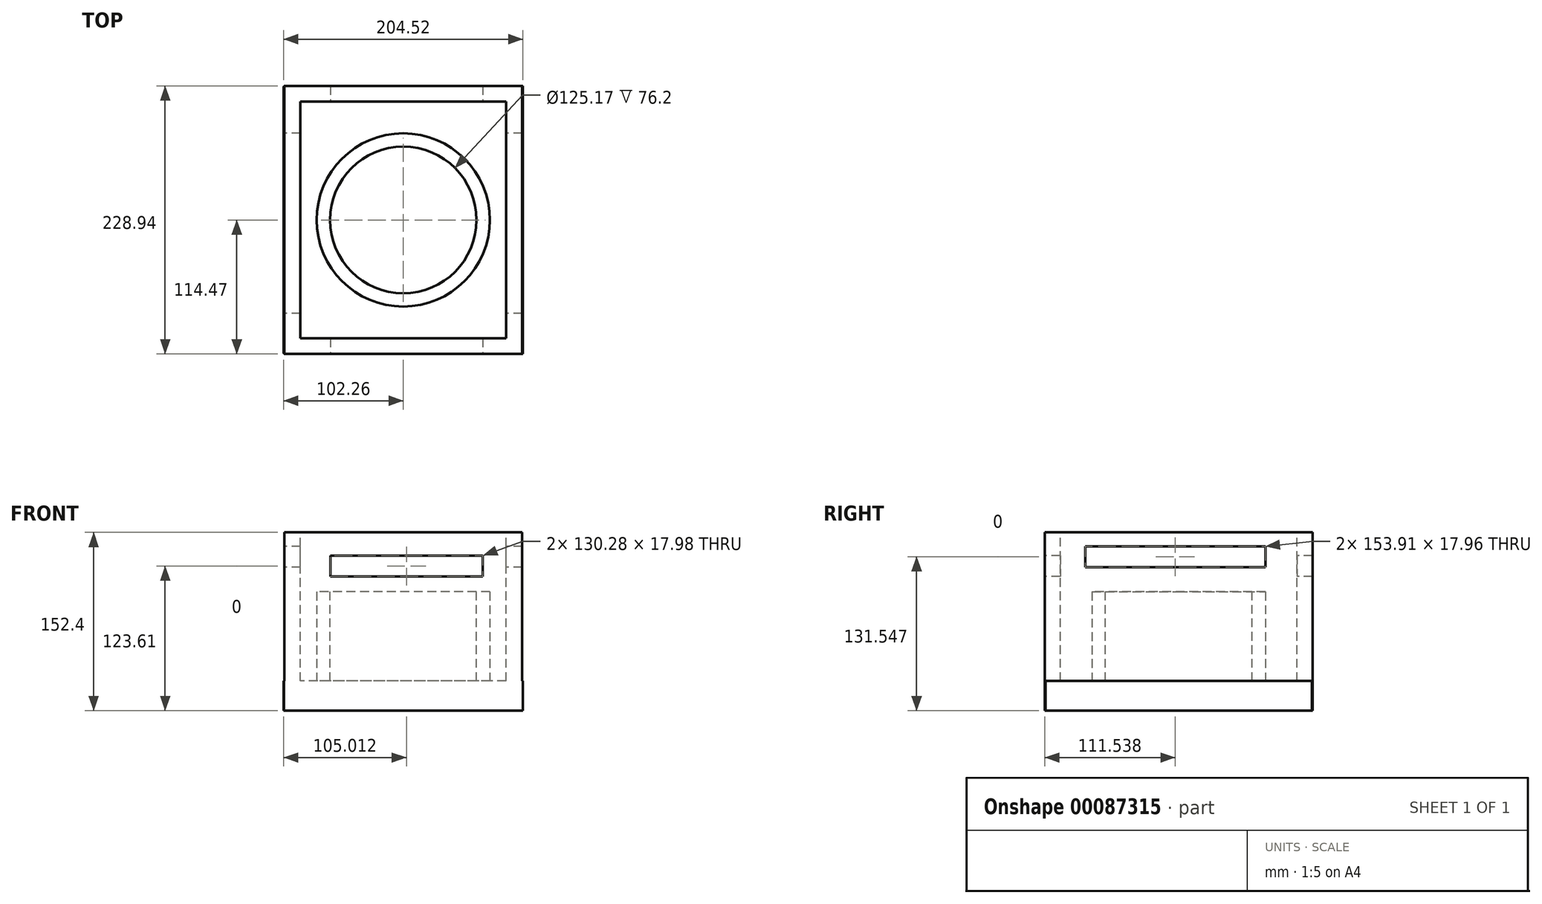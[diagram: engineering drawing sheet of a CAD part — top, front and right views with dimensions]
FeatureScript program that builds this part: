
annotation { "Feature Type Name" : "Feature", "Feature Type Description" : "" }
export const myFeature = defineFeature(function(context is Context, id is Id, definition is map)
    precondition{}
    {
        {
            var Q0;
            Q0=qCreatedBy(makeId("Top.planeOp"),FACE);
            var sketch = newSketch(context, id + "F0", { "sketchPlane" : qUnion([Q0])});
            skLineSegment(sketch, "E0.bottom", {"start": v(101.6, 114.47) * mm, "end": v(-101.6, 114.47) * mm});
            skLineSegment(sketch, "E0.top", {"start": v(101.6, -114.47) * mm, "end": v(-101.6, -114.47) * mm});
            skLineSegment(sketch, "E0.left", {"start": v(101.6, 114.47) * mm, "end": v(101.6, -114.47) * mm});
            skLineSegment(sketch, "E0.right", {"start": v(-101.6, 114.47) * mm, "end": v(-101.6, -114.47) * mm});
            skPoint(sketch, "E0.middle", {"position": v(0, 0) * mm});
            skSolve(sketch);
        }
        {
            var Q0;
            Q0 = qSketchRegion(id + "F0", true);
            extrude(context, id + "F1", {"entities" : qUnion([Q0]), "depth" : 152.4 * mm});
        }
        {
            var Q0;
            Q0=qCreatedBy(makeId("Top.planeOp"),FACE);
            var sketch = newSketch(context, id + "F2", { "sketchPlane" : qUnion([Q0])});
            skLineSegment(sketch, "E1.bottom", {"start": v(-87.87, -101.24) * mm, "end": v(87.87, -101.24) * mm});
            skLineSegment(sketch, "E1.top", {"start": v(-87.87, 101.24) * mm, "end": v(87.87, 101.24) * mm});
            skLineSegment(sketch, "E1.left", {"start": v(-87.87, -101.24) * mm, "end": v(-87.87, 101.24) * mm});
            skLineSegment(sketch, "E1.right", {"start": v(87.87, -101.24) * mm, "end": v(87.87, 101.24) * mm});
            skPoint(sketch, "E1.middle", {"position": v(0, 0) * mm});
            skSolve(sketch);
        }
        {
            var Q0;
            Q0 = qSketchRegion(id + "F2", true);
            extrude(context, id + "F3", {"entities" : qUnion([Q0]), "operationType" : NewBodyOperationType.REMOVE, "endBound" : BoundingType.SYMMETRIC, "oppositeDirection" : true, "depth" : 2540 * mm});
        }
        {
            var Q0;
            Q0=qCreatedBy(makeId("Top.planeOp"),FACE);
            var sketch = newSketch(context, id + "F4", { "sketchPlane" : qUnion([Q0])});
            skLineSegment(sketch, "E2.bottom", {"start": v(-102.11, -114.47) * mm, "end": v(102.11, -114.47) * mm});
            skLineSegment(sketch, "E2.top", {"start": v(-102.11, 114.47) * mm, "end": v(102.11, 114.47) * mm});
            skLineSegment(sketch, "E2.left", {"start": v(-102.11, -114.47) * mm, "end": v(-102.11, 114.47) * mm});
            skLineSegment(sketch, "E2.right", {"start": v(102.11, -114.47) * mm, "end": v(102.11, 114.47) * mm});
            skPoint(sketch, "E2.middle", {"position": v(0, 0) * mm});
            skSolve(sketch);
        }
        {
            var Q0;
            Q0 = qSketchRegion(id + "F4", true);
            extrude(context, id + "F5", {"entities" : qUnion([Q0]), "operationType" : NewBodyOperationType.ADD, "depth" : 25.4 * mm});
        }
        {
            var Q0;
            Q0=qCreatedBy(makeId("Top.planeOp"),FACE);
            var sketch = newSketch(context, id + "F6", { "sketchPlane" : qUnion([Q0])});
            skCircle(sketch, "E3", {"center": v(0, 0) * mm, "radius": 74.03 * mm});
            skSolve(sketch);
        }
        {
            var Q0;
            Q0 = qSketchRegion(id + "F6", true);
            extrude(context, id + "F7", {"entities" : qUnion([Q0]), "operationType" : NewBodyOperationType.ADD, "depth" : 101.6 * mm});
        }
        {
            var Q0;
            Q0=qCreatedBy(makeId("Top.planeOp"),FACE);
            var sketch = newSketch(context, id + "F8", { "sketchPlane" : qUnion([Q0])});
            skCircle(sketch, "E4", {"center": v(0, 0) * mm, "radius": 62.58 * mm});
            skSolve(sketch);
        }
        {
            var Q0;
            Q0 = qSketchRegion(id + "F8", true);
            extrude(context, id + "F9", {"entities" : qUnion([Q0]), "operationType" : NewBodyOperationType.REMOVE, "endBound" : BoundingType.SYMMETRIC, "oppositeDirection" : true, "depth" : 25400 * mm});
        }
        {
            var Q0;
            Q0=qCreatedBy(makeId("Top.planeOp"),FACE);
            var sketch = newSketch(context, id + "F10", { "sketchPlane" : qUnion([Q0])});
            skLineSegment(sketch, "E5.bottom", {"start": v(-102.26, 113.81) * mm, "end": v(102.26, 113.81) * mm});
            skLineSegment(sketch, "E5.top", {"start": v(-102.26, -113.81) * mm, "end": v(102.26, -113.81) * mm});
            skLineSegment(sketch, "E5.left", {"start": v(-102.26, 113.81) * mm, "end": v(-102.26, -113.81) * mm});
            skLineSegment(sketch, "E5.right", {"start": v(102.26, 113.81) * mm, "end": v(102.26, -113.81) * mm});
            skPoint(sketch, "E5.middle", {"position": v(0, 0) * mm});
            skSolve(sketch);
        }
        {
            var Q0;
            Q0 = qSketchRegion(id + "F10", true);
            extrude(context, id + "F11", {"entities" : qUnion([Q0]), "operationType" : NewBodyOperationType.ADD, "depth" : 25.4 * mm});
        }
        {
            var Q0;
            Q0=qCreatedBy(makeId("Front.planeOp"),FACE);
            var sketch = newSketch(context, id + "F12", { "sketchPlane" : qUnion([Q0])});
            skLineSegment(sketch, "E6.bottom", {"start": v(-62.39, 132.6) * mm, "end": v(67.9, 132.6) * mm});
            skLineSegment(sketch, "E6.top", {"start": v(-62.39, 114.62) * mm, "end": v(67.9, 114.62) * mm});
            skLineSegment(sketch, "E6.left", {"start": v(-62.39, 132.6) * mm, "end": v(-62.39, 114.62) * mm});
            skLineSegment(sketch, "E6.right", {"start": v(67.9, 132.6) * mm, "end": v(67.9, 114.62) * mm});
            skSolve(sketch);
        }
        {
            var Q0;
            Q0 = qSketchRegion(id + "F12", true);
            extrude(context, id + "F13", {"entities" : qUnion([Q0]), "operationType" : NewBodyOperationType.REMOVE, "endBound" : BoundingType.SYMMETRIC, "oppositeDirection" : true, "depth" : 25400 * mm});
        }
        {
            var Q0;
            Q0=qCreatedBy(makeId("Right.planeOp"),FACE);
            var sketch = newSketch(context, id + "F14", { "sketchPlane" : qUnion([Q0])});
            skLineSegment(sketch, "E7.bottom", {"start": v(74.02, 140.53) * mm, "end": v(-79.89, 140.53) * mm});
            skLineSegment(sketch, "E7.top", {"start": v(74.02, 122.57) * mm, "end": v(-79.89, 122.57) * mm});
            skLineSegment(sketch, "E7.left", {"start": v(74.02, 140.53) * mm, "end": v(74.02, 122.57) * mm});
            skLineSegment(sketch, "E7.right", {"start": v(-79.89, 140.53) * mm, "end": v(-79.89, 122.57) * mm});
            skSolve(sketch);
        }
        {
            var Q0;
            Q0 = qSketchRegion(id + "F14", true);
            extrude(context, id + "F15", {"entities" : qUnion([Q0]), "operationType" : NewBodyOperationType.REMOVE, "endBound" : BoundingType.SYMMETRIC, "depth" : 254000 * mm});
        }
    });
